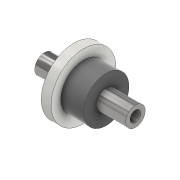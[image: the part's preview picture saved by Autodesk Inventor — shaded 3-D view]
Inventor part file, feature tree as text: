
AUTODESK INVENTOR PART (.ipt)
format: ipt  version: 2022 (Build 260153000, 153)  size: 162,304 bytes
history: native  units: mm
features: sketch x4, extrude x3, hole x1, mirror x1, plane x1
ambient origin geometry x8: Origin, YZ Plane, XZ Plane, XY Plane, X Axis, Y Axis, Z Axis, Center Point
bodies: Solid1 (feature_tree)
feature tree (10):
  extrude  "Extrusion1"  Depth=42.0mm TaperAngle=0.0deg
  hole  "Hole1"  [1 undecoded]
  mirror  "Mirror1"
  plane  "Work Plane2"
  extrude  "Extrusion2"  Depth=21.0mm
  extrude  "Extrusion3"  [1 undecoded]
  sketch  "Sketch1"  dims[d0=9.0mm d1=42.0mm d2=0.0mm]
  sketch  "Sketch2"  dims[d3=5.0mm d4=6.0mm d5=4.0mm d6=2.0mm d7=90.0deg d8=7.0mm d9=20.594885mm d10=30.0mm]
  sketch  "Sketch3"  dims[d11=4.5mm d12=0.0mm d13=21.0mm]
  sketch  "Sketch4"  dims[d15=0.0mm d17=-7.5mm d14=0.25mm d16=14.3117mm d18=20.594885mm d19=0.0625mm d20=0.75mm d21=0.375mm]
note: 2 required parameter values undecoded (feature->parameter linkage not recoverable at this tier; creation-order binding heuristic only, values carry confidence <= 0.55)
